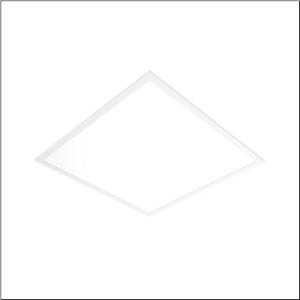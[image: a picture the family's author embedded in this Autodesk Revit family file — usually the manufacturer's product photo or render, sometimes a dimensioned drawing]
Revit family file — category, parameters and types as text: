
# Revit family: apollon_41_51mh11w72343
name_source: partatom
category: Lighting Fixtures
units: mm (PartAtom-declared; Revit-internal decimal feet)

## family parameters
Cut with Voids When Loaded = No
Host = Face
Light Source = No
Part Type = Normal
Room Calculation Point = No
Round Connector Dimension = Use Diameter
Shared = No

## types (1)
- Apollon 41 (1 x LED, 3500 lm, 28.5 W, 3000K)
    Apparent Load = 29 VA
    CIE Flux Codes = 61 87 97 100 100
    Color Rendering = 80
    Color Temperature = 3000K
    Default Elevation = 1800 mm
    Description = Apollon 41, office luminaire, primary optical cover: prismatic diffuser, of PS, light emission: direct distribution, primary light characteristic: symmetric, installation type: lay-in mounting, LED, rated luminous flux: 3.500lm, luminous efficacy: 123lm/W, light colour: 830, colour temperature: 3000K, control gear: ON/OFF, with terminal, 3-pole, mains connection: 220..240V, AC, 50/60Hz, housing, of aluminium section, traffic white (RAL 9016), module: M625, length: 620mm, width: 620mm, height: 60mm, recess depth: 180mm, housing upper side, of sheet steel, protection rating (complete): IP20, protection rating (lamp compartment, on room side): IP40, insulation class (complete): insulation class II (safety insulation), certification: CE, ENEC, impact resistance: IK03, permissible operating ambient temperature: -25..+40°C, packaging unit: 1 piece
    Height = 0 mm  [stored 0 ft]
    Lamp = 1 x LED
    Lamp Light Flux = 3500 lm
    Lamp Power = 28.5 W
    Lamp count = 1
    Length = 620 mm
    Luminous efficacy = 123 lm/W
    Manufacturer = Siteco
    ModVariant = No
    Model = 51MH11W72343
    Mounting Place = Ceiling
    Mounting Type = Recessed
    Number of Poles = 1
    OnlyDefault = Yes
    Power Factor = 1
    Product Name = Apollon 41
    Product group = office luminaire | ceiling recessed
    ProductGroupID = 400
    Protection Class = Protection class II
    Protection Degree = IP 20
    RLX_Detail_Level = 1
    RLX_Emergency_Light_Flux = 0 lm
    RLX_Emergency_Type = 0
    RLX_Emergency_Type_DB = No
    RlxData = <blob elided: 12237 chars, md5=98f15d91>
    Socket = socket
    Standby Power = 0 W
    System Light Flux = 3500 lm
    System Power = 29 W
    Type Comments = Product without accessories
    Type Image = l_1291024.jpg
    URL = http://relux.com
    VarID = ---
    Voltage = 0 V
    Weight = 0.00 kg
    Width = 620 mm

note: [stored X ft] marks values corroborated as IEEE doubles in the binary element streams (Revit-internal decimal feet)

## geometry (parser evidence)
native form markers: Sweep x9
no freeform markers — native parametric forms only
